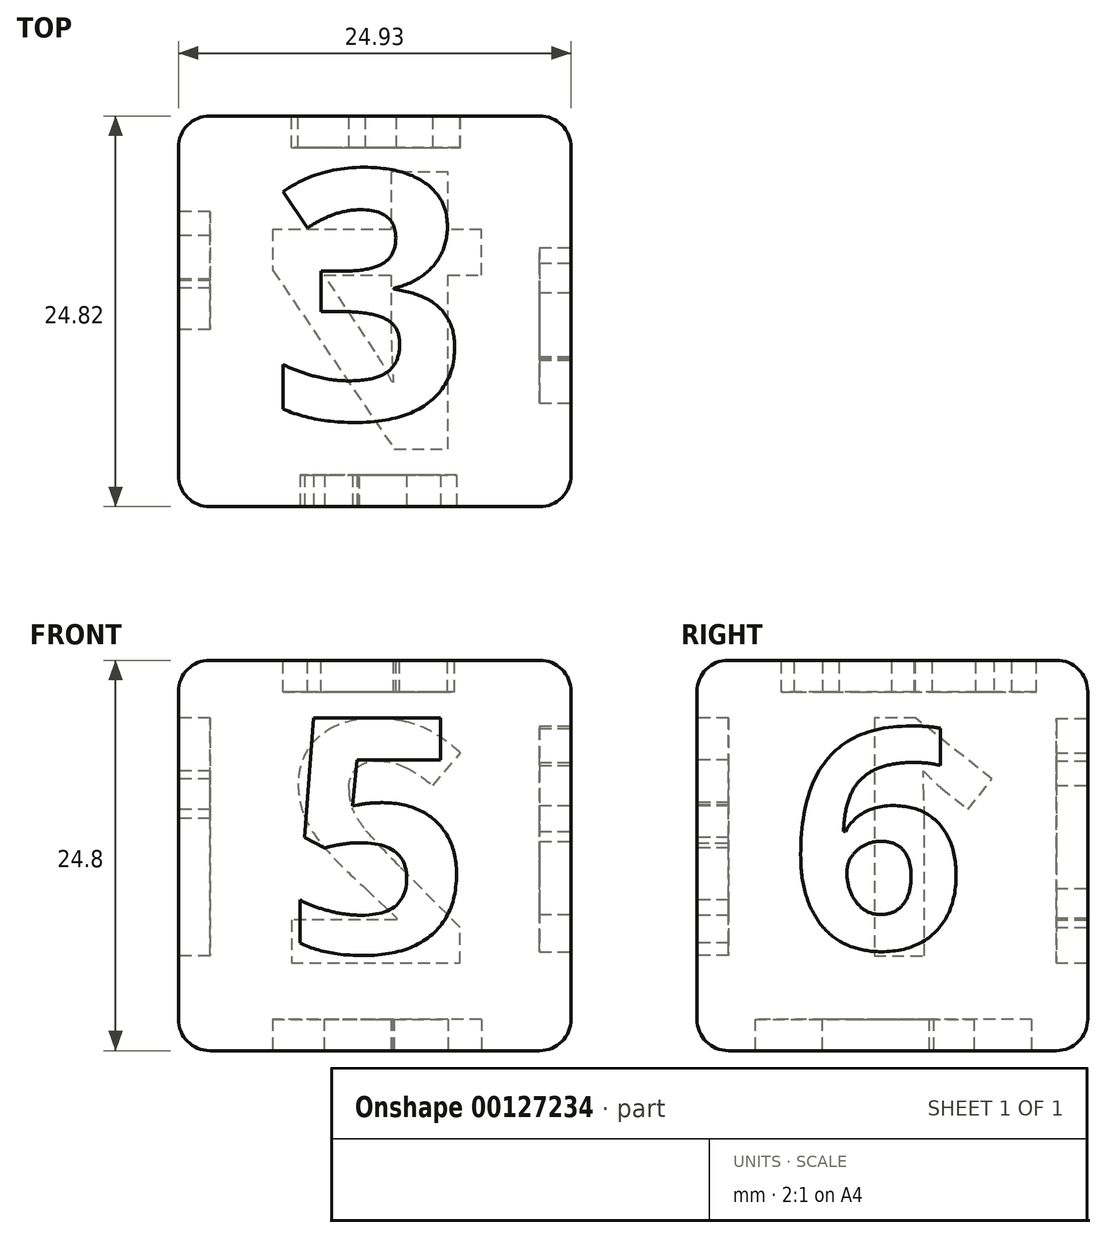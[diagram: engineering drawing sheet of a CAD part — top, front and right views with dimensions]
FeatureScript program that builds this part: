
annotation { "Feature Type Name" : "Feature", "Feature Type Description" : "" }
export const myFeature = defineFeature(function(context is Context, id is Id, definition is map)
    precondition{}
    {
        {
            var Q0;
            Q0=qCreatedBy(makeId("Top.planeOp"),FACE);
            var sketch = newSketch(context, id + "F0", { "sketchPlane" : qUnion([Q0])});
            skLineSegment(sketch, "E0.bottom", {"start": v(-21.47, 24.82) * mm, "end": v(3.46, 24.82) * mm});
            skLineSegment(sketch, "E0.top", {"start": v(-21.47, 0) * mm, "end": v(3.46, 0) * mm});
            skLineSegment(sketch, "E0.left", {"start": v(-21.47, 24.82) * mm, "end": v(-21.47, 0) * mm});
            skLineSegment(sketch, "E0.right", {"start": v(3.46, 24.82) * mm, "end": v(3.46, 0) * mm});
            skSolve(sketch);
        }
        {
            var Q0;
            Q0=makeQuery(id+"F0.imprint","IMPRINT",FACE,{"disambiguationData":[TD([[makeQuery(id+"F0.imprint","IMPRINT",EDGE,{"derivedFrom":sQuery(id+"F0.wireOp",EDGE,"E0.bottom")}),-1.0]])]});
            extrude(context, id + "F1", {"entities" : qUnion([Q0]), "depth" : 24.8 * mm});
        }
        {
            var Q0;
            Q0=makeQuery(id+"F1.opExtrude","SWEPT_FACE",FACE,{"disambiguationData":[OSD([sQuery(id+"F0.wireOp",EDGE,"E0.left")])]});
            var sketch = newSketch(context, id + "F2", { "sketchPlane" : qUnion([Q0])});
            skText(sketch, "E1", { "text": "1", "fontName": "OpenSans-Bold.ttf"});
            const initialGuessF2  = {"E1": [-0.02, 0.00602, 1, 0, 0.01523]};
            skSetInitialGuess(sketch, initialGuessF2);
            skSolve(sketch);
        }
        {
            var Q0;
            Q0 = qSketchRegion(id + "F2", true);
            extrude(context, id + "F3", {"entities" : qUnion([Q0]), "operationType" : NewBodyOperationType.REMOVE, "oppositeDirection" : true, "depth" : 2 * mm});
        }
        {
            var Q0;
            Q0=makeQuery(id+"F1.opExtrude","SWEPT_FACE",FACE,{"disambiguationData":[OSD([sQuery(id+"F0.wireOp",EDGE,"E0.right")])]});
            var sketch = newSketch(context, id + "F4", { "sketchPlane" : qUnion([Q0])});
            skText(sketch, "E2", { "text": "6\n", "fontName": "OpenSans-Bold.ttf"});
            const initialGuessF4  = {"E2": [0.0059, 0.00648, 1, 0, 0.0141]};
            skSetInitialGuess(sketch, initialGuessF4);
            skSolve(sketch);
        }
        {
            var Q0;
            Q0 = qSketchRegion(id + "F4", true);
            extrude(context, id + "F5", {"entities" : qUnion([Q0]), "operationType" : NewBodyOperationType.REMOVE, "oppositeDirection" : true, "depth" : 2 * mm});
        }
        {
            var Q0;
            Q0=makeQuery(id+"F1.opExtrude","CAP_FACE",FACE,{"disambiguationData":[OSD([sQuery(id+"F0.wireOp",EDGE,"E0.bottom"),sQuery(id+"F0.wireOp",EDGE,"E0.top"),sQuery(id+"F0.wireOp",EDGE,"E0.left"),sQuery(id+"F0.wireOp",EDGE,"E0.right")])],"isStart":false});
            var sketch = newSketch(context, id + "F6", { "sketchPlane" : qUnion([Q0])});
            skText(sketch, "E3", { "text": "3", "fontName": "OpenSans-Bold.ttf"});
            const initialGuessF6  = {"E3": [-0.01568, 0.00557, 1, 0, 0.0159]};
            skSetInitialGuess(sketch, initialGuessF6);
            skSolve(sketch);
        }
        {
            var Q0;
            Q0 = qSketchRegion(id + "F6", true);
            extrude(context, id + "F7", {"entities" : qUnion([Q0]), "operationType" : NewBodyOperationType.REMOVE, "oppositeDirection" : true, "depth" : 2 * mm});
        }
        {
            var Q0;
            Q0=makeQuery(id+"F1.opExtrude","SWEPT_FACE",FACE,{"disambiguationData":[OSD([sQuery(id+"F0.wireOp",EDGE,"E0.bottom")])]});
            var sketch = newSketch(context, id + "F8", { "sketchPlane" : qUnion([Q0])});
            skText(sketch, "E4", { "text": "2\n", "fontName": "OpenSans-Bold.ttf"});
            const initialGuessF8  = {"E4": [0.00273, 0.00557, 1, 0, 0.01545]};
            skSetInitialGuess(sketch, initialGuessF8);
            skSolve(sketch);
        }
        {
            var Q0;
            Q0 = qSketchRegion(id + "F8", true);
            extrude(context, id + "F9", {"entities" : qUnion([Q0]), "operationType" : NewBodyOperationType.REMOVE, "oppositeDirection" : true, "depth" : 2 * mm});
        }
        {
            var Q0;
            Q0=makeQuery(id+"F1.opExtrude","SWEPT_FACE",FACE,{"disambiguationData":[OSD([sQuery(id+"F0.wireOp",EDGE,"E0.top")])]});
            var sketch = newSketch(context, id + "F10", { "sketchPlane" : qUnion([Q0])});
            skText(sketch, "E5", { "text": "5", "fontName": "OpenSans-Bold.ttf"});
            const initialGuessF10  = {"E5": [-0.01477, 0.00625, 1, 0, 0.015]};
            skSetInitialGuess(sketch, initialGuessF10);
            skSolve(sketch);
        }
        {
            var Q0;
            Q0 = qSketchRegion(id + "F10", true);
            extrude(context, id + "F11", {"entities" : qUnion([Q0]), "operationType" : NewBodyOperationType.REMOVE, "oppositeDirection" : true, "depth" : 2 * mm});
        }
        {
            var Q0;
            Q0=makeQuery(id+"F1.opExtrude","CAP_FACE",FACE,{"disambiguationData":[OSD([sQuery(id+"F0.wireOp",EDGE,"E0.bottom"),sQuery(id+"F0.wireOp",EDGE,"E0.top"),sQuery(id+"F0.wireOp",EDGE,"E0.left"),sQuery(id+"F0.wireOp",EDGE,"E0.right")])],"isStart":true});
            var sketch = newSketch(context, id + "F12", { "sketchPlane" : qUnion([Q0])});
            skText(sketch, "E6", { "text": "4", "fontName": "OpenSans-Bold.ttf"});
            const initialGuessF12  = {"E6": [-0.0159, -0.02125, 1, 0, 0.01773]};
            skSetInitialGuess(sketch, initialGuessF12);
            skSolve(sketch);
        }
        {
            var Q0;
            Q0 = qSketchRegion(id + "F12", true);
            extrude(context, id + "F13", {"entities" : qUnion([Q0]), "operationType" : NewBodyOperationType.REMOVE, "oppositeDirection" : true, "depth" : 2 * mm});
        }
        {
            var Q0;
            Q0=makeQuery(id+"F1.opExtrude","CAP_EDGE",EDGE,{"disambiguationData":[OSD([sQuery(id+"F0.wireOp",EDGE,"E0.top")])],"isStart":false});
            var Q1;
            Q1=makeQuery(id+"F1.opExtrude","CAP_EDGE",EDGE,{"disambiguationData":[OSD([sQuery(id+"F0.wireOp",EDGE,"E0.right")])],"isStart":false});
            var Q2;
            Q2=makeQuery(id+"F1.opExtrude","SWEPT_EDGE",EDGE,{"disambiguationData":[OSD([sQuery(id+"F0.wireOp",EDGE,"E0.top"),sQuery(id+"F0.wireOp",EDGE,"E0.right")])]});
            var Q3;
            Q3=makeQuery(id+"F1.opExtrude","CAP_EDGE",EDGE,{"disambiguationData":[OSD([sQuery(id+"F0.wireOp",EDGE,"E0.top")])],"isStart":true});
            var Q4;
            Q4=makeQuery(id+"F1.opExtrude","SWEPT_EDGE",EDGE,{"disambiguationData":[OSD([sQuery(id+"F0.wireOp",EDGE,"E0.top"),sQuery(id+"F0.wireOp",EDGE,"E0.left")])]});
            var Q5;
            Q5=makeQuery(id+"F1.opExtrude","CAP_EDGE",EDGE,{"disambiguationData":[OSD([sQuery(id+"F0.wireOp",EDGE,"E0.right")])],"isStart":true});
            var Q6;
            Q6=makeQuery(id+"F1.opExtrude","CAP_EDGE",EDGE,{"disambiguationData":[OSD([sQuery(id+"F0.wireOp",EDGE,"E0.bottom")])],"isStart":true});
            var Q7;
            Q7=makeQuery(id+"F1.opExtrude","CAP_EDGE",EDGE,{"disambiguationData":[OSD([sQuery(id+"F0.wireOp",EDGE,"E0.left")])],"isStart":true});
            var Q8;
            Q8=makeQuery(id+"F1.opExtrude","SWEPT_EDGE",EDGE,{"disambiguationData":[OSD([sQuery(id+"F0.wireOp",EDGE,"E0.bottom"),sQuery(id+"F0.wireOp",EDGE,"E0.right")])]});
            var Q9;
            Q9=makeQuery(id+"F1.opExtrude","CAP_EDGE",EDGE,{"disambiguationData":[OSD([sQuery(id+"F0.wireOp",EDGE,"E0.left")])],"isStart":false});
            var Q10;
            Q10=makeQuery(id+"F1.opExtrude","SWEPT_EDGE",EDGE,{"disambiguationData":[OSD([sQuery(id+"F0.wireOp",EDGE,"E0.bottom"),sQuery(id+"F0.wireOp",EDGE,"E0.left")])]});
            var Q11;
            Q11=makeQuery(id+"F1.opExtrude","CAP_EDGE",EDGE,{"disambiguationData":[OSD([sQuery(id+"F0.wireOp",EDGE,"E0.bottom")])],"isStart":false});
            fillet(context, id + "F14", {"entities" : qUnion([Q0, Q1, Q2, Q3, Q4, Q5, Q6, Q7, Q8, Q9, Q10, Q11]), "radius" : 2 * mm, "tangentPropagation" : true, "allowEdgeOverflow" : false});
        }
    });
